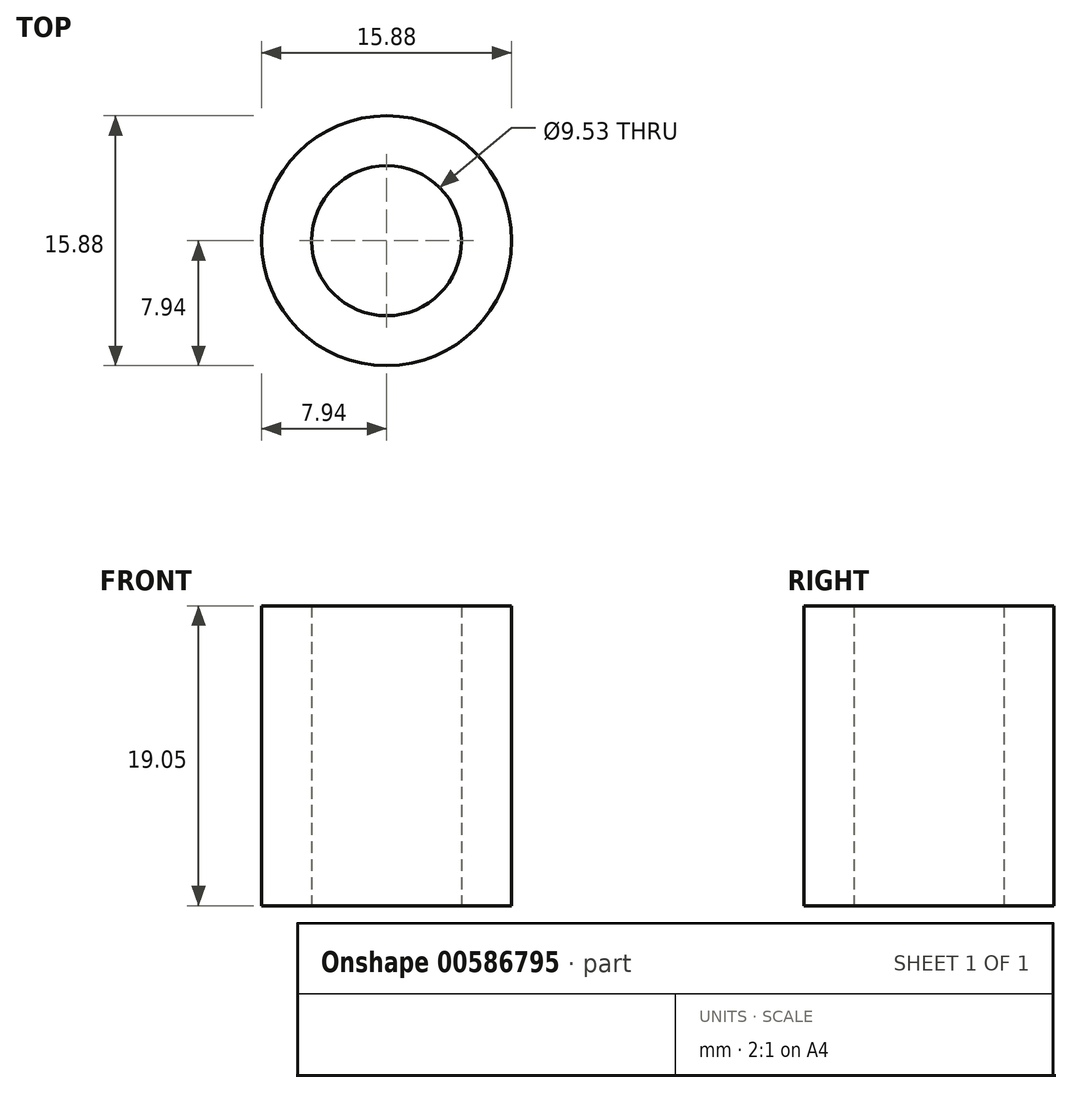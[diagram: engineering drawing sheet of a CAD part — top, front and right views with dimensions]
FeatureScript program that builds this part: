
annotation { "Feature Type Name" : "Feature", "Feature Type Description" : "" }
export const myFeature = defineFeature(function(context is Context, id is Id, definition is map)
    precondition{}
    {
        {
            var Q0;
            Q0=qCreatedBy(makeId("Top.planeOp"),FACE);
            var sketch = newSketch(context, id + "F0", { "sketchPlane" : qUnion([Q0])});
            skCircle(sketch, "E0", {"center": v(0, 0) * mm, "radius": 7.94 * mm});
            skCircle(sketch, "E1", {"center": v(0, 0) * mm, "radius": 4.76 * mm});
            skSolve(sketch);
        }
        {
            var Q0;
            Q0 = qSketchRegion(id + "F0", true);
            extrude(context, id + "F1", {"entities" : qUnion([Q0]), "depth" : 19.05 * mm, "offsetDistance" : 25.4 * mm});
        }
    });
